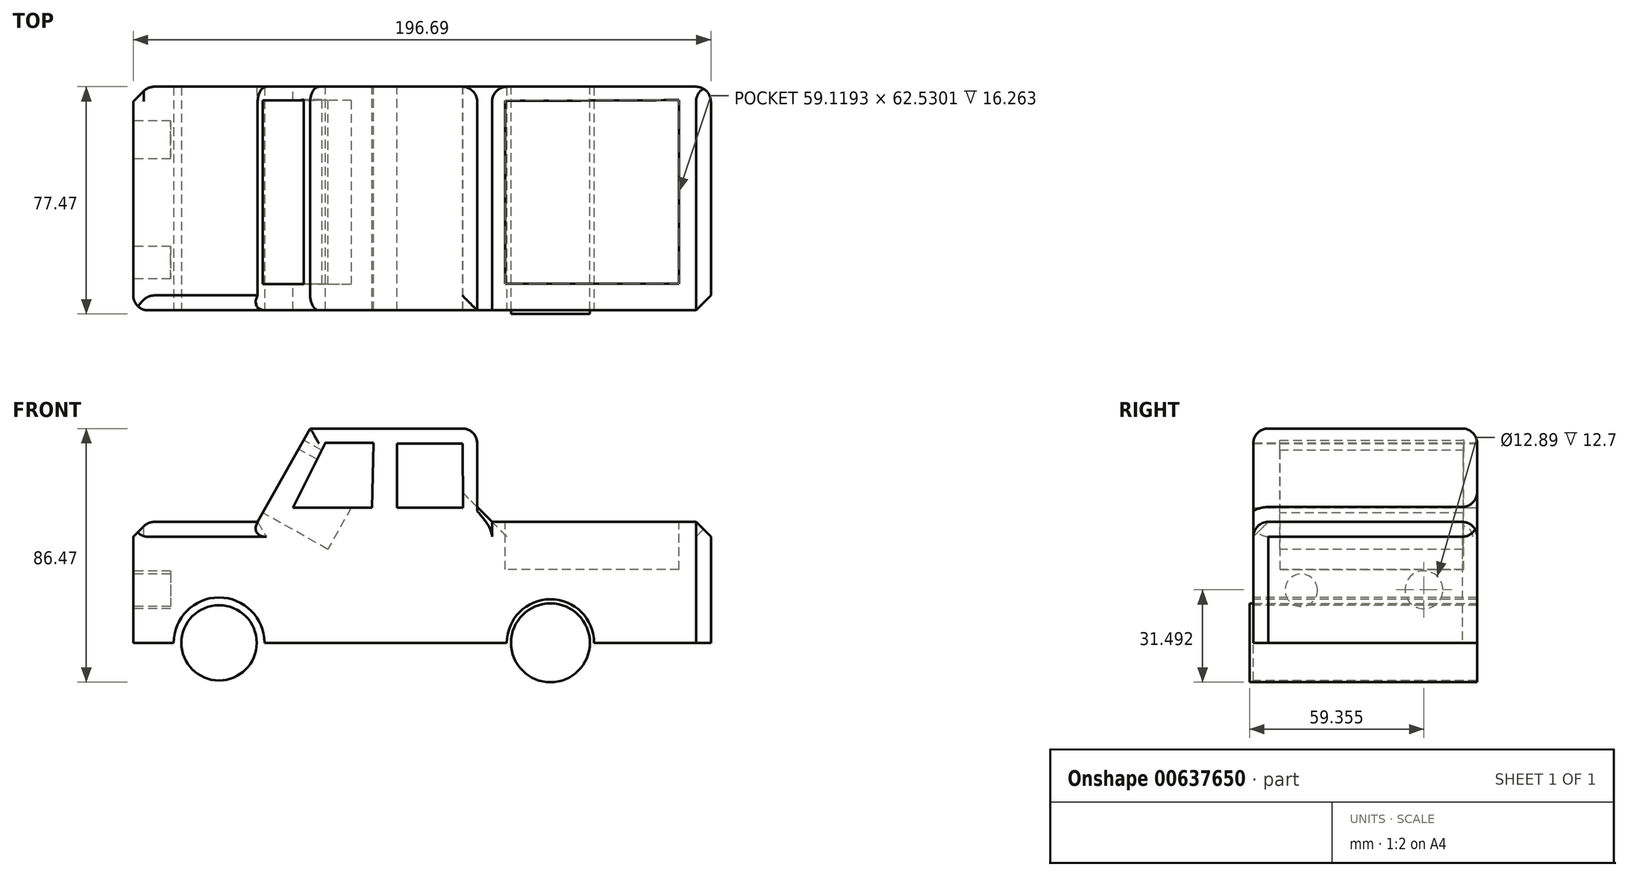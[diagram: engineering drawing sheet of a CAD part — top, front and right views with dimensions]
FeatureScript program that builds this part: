
annotation { "Feature Type Name" : "Feature", "Feature Type Description" : "" }
export const myFeature = defineFeature(function(context is Context, id is Id, definition is map)
    precondition{}
    {
        {
            var Q0;
            Q0=qCreatedBy(makeId("Front.planeOp"),FACE);
            var sketch = newSketch(context, id + "F0", { "sketchPlane" : qUnion([Q0])});
            skLineSegment(sketch, "E0", {"start": v(-75.18, -14.21) * mm, "end": v(-32.83, -14.21) * mm});
            skLineSegment(sketch, "E1", {"start": v(-32.83, -14.21) * mm, "end": v(-14.92, 17.62) * mm});
            skLineSegment(sketch, "E2", {"start": v(-75.18, -14.21) * mm, "end": v(-66.65, -14.21) * mm});
            skLineSegment(sketch, "E3", {"start": v(-14.92, 17.62) * mm, "end": v(41.92, 17.62) * mm});
            skLineSegment(sketch, "E4", {"start": v(41.92, 17.62) * mm, "end": v(41.92, -14.21) * mm});
            skLineSegment(sketch, "E5", {"start": v(41.92, -14.21) * mm, "end": v(-32.83, -14.21) * mm});
            skLineSegment(sketch, "E6", {"start": v(41.92, -14.21) * mm, "end": v(121.5, -14.21) * mm});
            skLineSegment(sketch, "E7", {"start": v(121.5, -14.21) * mm, "end": v(121.5, -37.52) * mm});
            skLineSegment(sketch, "E8", {"start": v(-75.18, -14.21) * mm, "end": v(-75.18, -55.42) * mm});
            skLineSegment(sketch, "E9", {"start": v(-75.18, -55.42) * mm, "end": v(121.5, -55.42) * mm});
            skLineSegment(sketch, "E10", {"start": v(121.5, -55.42) * mm, "end": v(121.5, -37.52) * mm});
            skCircle(sketch, "E11", {"center": v(-45.96, -55.42) * mm, "radius": 13.02 * mm});
            skCircle(sketch, "E12", {"center": v(66.89, -55.42) * mm, "radius": 13.43 * mm});
            skLineSegment(sketch, "E13", {"start": v(-9.74, 12.79) * mm, "end": v(-20.85, -9.38) * mm});
            skLineSegment(sketch, "E14", {"start": v(-9.74, 12.79) * mm, "end": v(6.58, 12.79) * mm});
            skLineSegment(sketch, "E15", {"start": v(-20.85, -9.38) * mm, "end": v(6.1, -9.38) * mm});
            skLineSegment(sketch, "E16", {"start": v(6.1, -9.38) * mm, "end": v(6.58, 12.79) * mm});
            skLineSegment(sketch, "E17", {"start": v(14.61, 12.44) * mm, "end": v(14.61, -9.35) * mm});
            skLineSegment(sketch, "E18", {"start": v(14.61, 12.44) * mm, "end": v(37, 12.44) * mm});
            skLineSegment(sketch, "E19", {"start": v(14.61, -9.35) * mm, "end": v(37.12, -9.35) * mm});
            skLineSegment(sketch, "E20", {"start": v(37, 12.44) * mm, "end": v(37.12, -9.35) * mm});
            skSolve(sketch);
        }
        {
            var Q0;
            Q0 = qSketchRegion(id + "F0", true);
            extrude(context, id + "F1", {"entities" : qUnion([Q0]), "depth" : 76.2 * mm, "offsetDistance" : 25.4 * mm});
        }
        {
            var Q0;
            Q0=makeQuery(id+"F1.opExtrude","CAP_EDGE",EDGE,{"disambiguationData":[OSD([sQuery(id+"F0.wireOp",EDGE,"E3")])],"isStart":false});
            var Q1;
            Q1=makeQuery(id+"F1.opExtrude","SWEPT_EDGE",EDGE,{"disambiguationData":[OSD([sQuery(id+"F0.wireOp",EDGE,"E3"),sQuery(id+"F0.wireOp",EDGE,"E4")])]});
            var Q2;
            Q2=makeQuery(id+"F1.opExtrude","CAP_EDGE",EDGE,{"disambiguationData":[OSD([sQuery(id+"F0.wireOp",EDGE,"E1")])],"isStart":false});
            fillet(context, id + "F2", {"entities" : qUnion([Q0, Q1, Q2]), "radius" : 5.08 * mm, "tangentPropagation" : true, "allowEdgeOverflow" : false});
        }
        {
            var Q0;
            Q0=makeQuery(id+"F1.opExtrude","CAP_EDGE",EDGE,{"disambiguationData":[OSD([sQuery(id+"F0.wireOp",EDGE,"E0"),sQuery(id+"F0.wireOp",EDGE,"E2")])],"isStart":false});
            chamfer(context, id + "F3", {"entities" : qUnion([Q0]), "width" : 5.08 * mm, "tangentPropagation" : true});
        }
        {
            var Q0;
            Q0=makeQuery(id+"F1.opExtrude","CAP_EDGE",EDGE,{"disambiguationData":[OSD([sQuery(id+"F0.wireOp",EDGE,"E8")])],"isStart":false});
            fillet(context, id + "F4", {"entities" : qUnion([Q0]), "radius" : 5.08 * mm, "tangentPropagation" : true, "allowEdgeOverflow" : false});
        }
        {
            var Q0;
            Q0=makeQuery(id+"F1.opExtrude","CAP_EDGE",EDGE,{"disambiguationData":[OSD([sQuery(id+"F0.wireOp",EDGE,"E6")])],"isStart":false});
            fillet(context, id + "F5", {"entities" : qUnion([Q0]), "radius" : 5.08 * mm, "tangentPropagation" : true, "allowEdgeOverflow" : false});
        }
        {
            var Q0;
            {var subQ0=sQuery(id+"F0.wireOp",EDGE,"E6");Q0=makeQuery(id+"F5.opFillet","BLEND_EDGE",EDGE,{"blendedFrom":[makeQuery(id+"F1.opExtrude","CAP_EDGE",EDGE,{"disambiguationData":[OSD([subQ0])],"isStart":false}),makeQuery(id+"F1.opExtrude","SWEPT_FACE",FACE,{"disambiguationData":[OSD([subQ0])]})],"blendedInto":[makeQuery(id+"F1.opExtrude","SWEPT_FACE",FACE,{"disambiguationData":[OSD([subQ0])]})]});}
            var Q1;
            Q1=makeQuery(id+"F5.opFillet","BLEND_FACE",FACE,{"disambiguationData":[OSD([sQuery(id+"F0.wireOp",EDGE,"E6")])]});
            chamfer(context, id + "F6", {"entities" : qUnion([Q0, Q1]), "width" : 5.08 * mm, "tangentPropagation" : true});
        }
        {
            var Q0;
            Q0=qCreatedBy(makeId("Top.planeOp"),FACE);
            var sketch = newSketch(context, id + "F7", { "sketchPlane" : qUnion([Q0])});
            skLineSegment(sketch, "E21", {"start": v(51.5, -4.83) * mm, "end": v(51.5, -67.08) * mm});
            skLineSegment(sketch, "E22", {"start": v(51.5, -67.08) * mm, "end": v(110.62, -67.08) * mm});
            skLineSegment(sketch, "E23", {"start": v(110.62, -67.08) * mm, "end": v(110.62, -4.55) * mm});
            skLineSegment(sketch, "E24", {"start": v(110.62, -4.55) * mm, "end": v(51.5, -4.83) * mm});
            skSolve(sketch);
        }
        {
            var Q0;
            Q0 = qSketchRegion(id + "F7", true);
            extrude(context, id + "F8", {"entities" : qUnion([Q0]), "operationType" : NewBodyOperationType.REMOVE, "oppositeDirection" : true, "depth" : 30.48 * mm, "offsetDistance" : 25.4 * mm});
        }
        {
            var Q0;
            Q0=makeQuery(id+"F1.opExtrude","SWEPT_FACE",FACE,{"disambiguationData":[OSD([sQuery(id+"F0.wireOp",EDGE,"E1")])]});
            var sketch = newSketch(context, id + "F9", { "sketchPlane" : qUnion([Q0])});
            skLineSegment(sketch, "E25", {"start": v(4.69, 0) * mm, "end": v(4.69, -24.9) * mm});
            skLineSegment(sketch, "E26", {"start": v(4.69, -24.9) * mm, "end": v(67.22, -24.9) * mm});
            skLineSegment(sketch, "E27", {"start": v(67.22, -24.9) * mm, "end": v(67.22, 3.48) * mm});
            skLineSegment(sketch, "E28", {"start": v(67.22, 3.48) * mm, "end": v(4.4, 3.48) * mm});
            skLineSegment(sketch, "E29", {"start": v(4.4, 3.48) * mm, "end": v(4.69, 0) * mm});
            skSolve(sketch);
        }
        {
            var Q0;
            Q0=makeQuery(id+"F9.imprint","IMPRINT",FACE,{"disambiguationData":[TD([[makeQuery(id+"F9.imprint","IMPRINT",EDGE,{"derivedFrom":sQuery(id+"F9.wireOp",EDGE,"E25")}),1.0]])]});
            extrude(context, id + "F10", {"entities" : qUnion([Q0]), "operationType" : NewBodyOperationType.REMOVE, "oppositeDirection" : true, "depth" : 25.4 * mm, "offsetDistance" : 25.4 * mm});
        }
        {
            var Q0;
            Q0=sQuery(id+"F0.wireOp",EDGE,"E11");
            extrude(context, id + "F11", {"bodyType" : ToolBodyType.SURFACE, "surfaceEntities" : qUnion([Q0]), "depth" : 76.2 * mm, "offsetDistance" : 25.4 * mm});
        }
        {
            var Q0;
            Q0=makeQuery(id+"F1.opExtrude","CAP_FACE",FACE,{"disambiguationData":[OSD([sQuery(id+"F0.wireOp",EDGE,"E0"),sQuery(id+"F0.wireOp",EDGE,"E1"),sQuery(id+"F0.wireOp",EDGE,"E2"),sQuery(id+"F0.wireOp",EDGE,"E3"),sQuery(id+"F0.wireOp",EDGE,"E4"),sQuery(id+"F0.wireOp",EDGE,"E6"),sQuery(id+"F0.wireOp",EDGE,"E7"),sQuery(id+"F0.wireOp",EDGE,"E8"),sQuery(id+"F0.wireOp",EDGE,"E9"),sQuery(id+"F0.wireOp",EDGE,"E10"),sQuery(id+"F0.wireOp",EDGE,"E11"),sQuery(id+"F0.wireOp",EDGE,"E12"),sQuery(id+"F0.wireOp",EDGE,"E13"),sQuery(id+"F0.wireOp",EDGE,"E14"),sQuery(id+"F0.wireOp",EDGE,"E15"),sQuery(id+"F0.wireOp",EDGE,"E16"),sQuery(id+"F0.wireOp",EDGE,"E17"),sQuery(id+"F0.wireOp",EDGE,"E18"),sQuery(id+"F0.wireOp",EDGE,"E19"),sQuery(id+"F0.wireOp",EDGE,"E20")])],"isStart":false});
            var sketch = newSketch(context, id + "F12", { "sketchPlane" : qUnion([Q0])});
            skCircle(sketch, "E30", {"center": v(-45.96, -55.42) * mm, "radius": 12.82 * mm});
            skCircle(sketch, "E31", {"center": v(-45.96, -55.42) * mm, "radius": 15.45 * mm});
            skSolve(sketch);
        }
        {
            var Q0;
            Q0 = qSketchRegion(id + "F12", true);
            var Q1;
            Q1 = qSketchRegion(id + "F14", true);
            extrude(context, id + "F13", {"entities" : qUnion([Q0, Q1]), "operationType" : NewBodyOperationType.REMOVE, "oppositeDirection" : true, "depth" : 76.2 * mm, "offsetDistance" : 25.4 * mm});
        }
        {
            var Q0;
            {var subQ0=sQuery(id+"F0.wireOp",EDGE,"E18");var subQ1=sQuery(id+"F0.wireOp",EDGE,"E17");var subQ2=sQuery(id+"F0.wireOp",EDGE,"E2");var subQ3=sQuery(id+"F0.wireOp",EDGE,"E0");var subQ4=sQuery(id+"F0.wireOp",EDGE,"E16");var subQ5=sQuery(id+"F0.wireOp",EDGE,"E13");var subQ6=sQuery(id+"F0.wireOp",EDGE,"E12");var subQ7=sQuery(id+"F0.wireOp",EDGE,"E6");var subQ8=sQuery(id+"F0.wireOp",EDGE,"E15");var subQ9=sQuery(id+"F0.wireOp",EDGE,"E4");var subQ10=sQuery(id+"F0.wireOp",EDGE,"E11");var subQ11=sQuery(id+"F0.wireOp",EDGE,"E9");var subQ12=sQuery(id+"F0.wireOp",EDGE,"E1");var subQ13=sQuery(id+"F0.wireOp",EDGE,"E8");var subQ14=sQuery(id+"F0.wireOp",EDGE,"E3");var subQ15=sQuery(id+"F0.wireOp",EDGE,"E10");var subQ16=sQuery(id+"F0.wireOp",EDGE,"E19");var subQ17=sQuery(id+"F0.wireOp",EDGE,"E20");var subQ18=sQuery(id+"F0.wireOp",EDGE,"E7");Q0=makeQuery(id+"F13.boolean.opBoolean","SPLIT",FACE,{"disambiguationData":[TD([makeQuery(id+"F1.opExtrude","SWEPT_FACE",FACE,{"disambiguationData":[OSD([subQ9])]})])],"derivedFrom":makeQuery(id+"F1.opExtrude","CAP_FACE",FACE,{"disambiguationData":[OSD([subQ3,subQ12,subQ2,subQ14,subQ9,subQ7,subQ18,subQ13,subQ11,subQ15,subQ10,subQ6,subQ5,sQuery(id+"F0.wireOp",EDGE,"E14"),subQ8,subQ4,subQ1,subQ0,subQ16,subQ17])],"isStart":false})});}
            var sketch = newSketch(context, id + "F14", { "sketchPlane" : qUnion([Q0])});
            skCircle(sketch, "E32", {"center": v(66.89, -55.42) * mm, "radius": 14.85 * mm});
            skSolve(sketch);
        }
        {
            var Q0;
            Q0 = qSketchRegion(id + "F14", true);
            extrude(context, id + "F15", {"entities" : qUnion([Q0]), "operationType" : NewBodyOperationType.REMOVE, "oppositeDirection" : true, "depth" : 76.2 * mm, "offsetDistance" : 25.4 * mm});
        }
        {
            var Q0;
            Q0 = qSketchRegion(id + "F14", true);
            extrude(context, id + "F16", {"entities" : qUnion([Q0]), "operationType" : NewBodyOperationType.REMOVE, "oppositeDirection" : true, "depth" : 76.2 * mm, "offsetDistance" : 25.4 * mm});
        }
        {
            var Q0;
            {var subQ0=sQuery(id+"F0.wireOp",EDGE,"E12");var subQ1=sQuery(id+"F0.wireOp",EDGE,"E9");var subQ2=makeQuery(id+"F0.imprint","INTERSECT",VERTEX,{"disambiguationData":[OD(0.0)],"derivedFrom":[subQ1,subQ0]});Q0=makeQuery(id+"F0.imprint","IMPRINT",FACE,{"disambiguationData":[TD([[makeQuery(id+"F0.imprint","IMPRINT",EDGE,{"disambiguationData":[TD([[subQ2,-1.0]])],"derivedFrom":subQ1}),-1.0]])]});}
            var Q1;
            {var subQ0=sQuery(id+"F0.wireOp",EDGE,"E12");var subQ1=sQuery(id+"F0.wireOp",EDGE,"E9");var subQ2=makeQuery(id+"F0.imprint","INTERSECT",VERTEX,{"disambiguationData":[OD(0.0)],"derivedFrom":[subQ1,subQ0]});Q1=makeQuery(id+"F0.imprint","IMPRINT",FACE,{"disambiguationData":[TD([[makeQuery(id+"F0.imprint","IMPRINT",EDGE,{"disambiguationData":[TD([[subQ2,-1.0]])],"derivedFrom":subQ1}),1.0]])]});}
            extrude(context, id + "F17", {"entities" : qUnion([Q0, Q1]), "depth" : 77.47 * mm, "offsetDistance" : 25.4 * mm});
        }
        {
            var Q0;
            Q0=makeQuery(id+"F1.opExtrude","CAP_EDGE",EDGE,{"disambiguationData":[OSD([sQuery(id+"F0.wireOp",EDGE,"E1")])],"isStart":true});
            var Q1;
            Q1=makeQuery(id+"F1.opExtrude","CAP_EDGE",EDGE,{"disambiguationData":[OSD([sQuery(id+"F0.wireOp",EDGE,"E3")])],"isStart":true});
            var Q2;
            Q2=makeQuery(id+"F1.opExtrude","CAP_EDGE",EDGE,{"disambiguationData":[OSD([sQuery(id+"F0.wireOp",EDGE,"E0"),sQuery(id+"F0.wireOp",EDGE,"E2")])],"isStart":true});
            fillet(context, id + "F18", {"entities" : qUnion([Q0, Q1, Q2]), "radius" : 5.08 * mm, "tangentPropagation" : true, "allowEdgeOverflow" : false});
        }
        {
            var Q0;
            Q0=makeQuery(id+"F1.opExtrude","CAP_EDGE",EDGE,{"disambiguationData":[OSD([sQuery(id+"F0.wireOp",EDGE,"E8")])],"isStart":true});
            chamfer(context, id + "F19", {"entities" : qUnion([Q0]), "width" : 5.08 * mm, "tangentPropagation" : true});
        }
        {
            var Q0;
            Q0=makeQuery(id+"F1.opExtrude","CAP_EDGE",EDGE,{"disambiguationData":[OSD([sQuery(id+"F0.wireOp",EDGE,"E6")])],"isStart":true});
            var Q1;
            {var subQ0=sQuery(id+"F0.wireOp",EDGE,"E7");var subQ1=sQuery(id+"F0.wireOp",EDGE,"E6");var subQ2=sQuery(id+"F0.wireOp",EDGE,"E4");var subQ3=sQuery(id+"F0.wireOp",EDGE,"E20");var subQ4=sQuery(id+"F0.wireOp",EDGE,"E19");var subQ5=sQuery(id+"F0.wireOp",EDGE,"E18");var subQ6=sQuery(id+"F0.wireOp",EDGE,"E17");var subQ7=sQuery(id+"F0.wireOp",EDGE,"E16");var subQ8=sQuery(id+"F0.wireOp",EDGE,"E15");var subQ9=sQuery(id+"F0.wireOp",EDGE,"E14");var subQ10=sQuery(id+"F0.wireOp",EDGE,"E13");var subQ11=sQuery(id+"F0.wireOp",EDGE,"E12");var subQ12=sQuery(id+"F0.wireOp",EDGE,"E3");var subQ13=sQuery(id+"F0.wireOp",EDGE,"E1");var subQ14=sQuery(id+"F0.wireOp",EDGE,"E2");var subQ15=sQuery(id+"F0.wireOp",EDGE,"E0");var subQ16=sQuery(id+"F0.wireOp",EDGE,"E10");var subQ17=sQuery(id+"F0.wireOp",EDGE,"E8");var subQ18=sQuery(id+"F0.wireOp",EDGE,"E9");var subQ19=sQuery(id+"F0.wireOp",EDGE,"E11");Q1=makeQuery(id+"F18.opFillet","BLEND_EDGE",EDGE,{"blendedFrom":[makeQuery(id+"F1.opExtrude","CAP_EDGE",EDGE,{"disambiguationData":[OSD([subQ13])],"isStart":true}),makeQuery(id+"F13.boolean.opBoolean","SPLIT",FACE,{"disambiguationData":[TD([makeQuery(id+"F1.opExtrude","SWEPT_FACE",FACE,{"disambiguationData":[OSD([subQ13])]})])],"derivedFrom":makeQuery(id+"F1.opExtrude","CAP_FACE",FACE,{"disambiguationData":[OSD([subQ15,subQ13,subQ14,subQ12,subQ2,subQ1,subQ0,subQ17,subQ18,subQ16,subQ19,subQ11,subQ10,subQ9,subQ8,subQ7,subQ6,subQ5,subQ4,subQ3])],"isStart":true})})],"blendedInto":[makeQuery(id+"F13.boolean.opBoolean","SPLIT",FACE,{"disambiguationData":[TD([makeQuery(id+"F1.opExtrude","SWEPT_FACE",FACE,{"disambiguationData":[OSD([subQ13])]})])],"derivedFrom":makeQuery(id+"F1.opExtrude","CAP_FACE",FACE,{"disambiguationData":[OSD([subQ15,subQ13,subQ14,subQ12,subQ2,subQ1,subQ0,subQ17,subQ18,subQ16,subQ19,subQ11,subQ10,subQ9,subQ8,subQ7,subQ6,subQ5,subQ4,subQ3])],"isStart":true})})]});}
            fillet(context, id + "F20", {"entities" : qUnion([Q0, Q1]), "radius" : 5.08 * mm, "tangentPropagation" : true, "allowEdgeOverflow" : false});
        }
        {
            var Q0;
            Q0=makeQuery(id+"F1.opExtrude","CAP_EDGE",EDGE,{"disambiguationData":[OSD([sQuery(id+"F0.wireOp",EDGE,"E7"),sQuery(id+"F0.wireOp",EDGE,"E10")])],"isStart":true});
            fillet(context, id + "F21", {"entities" : qUnion([Q0]), "radius" : 5.08 * mm, "tangentPropagation" : true, "allowEdgeOverflow" : false});
        }
        {
            var Q0;
            {var subQ0=sQuery(id+"F0.wireOp",EDGE,"E7");var subQ1=sQuery(id+"F0.wireOp",EDGE,"E6");var subQ2=sQuery(id+"F0.wireOp",EDGE,"E4");var subQ3=sQuery(id+"F0.wireOp",EDGE,"E20");var subQ4=sQuery(id+"F0.wireOp",EDGE,"E19");var subQ5=sQuery(id+"F0.wireOp",EDGE,"E18");var subQ6=sQuery(id+"F0.wireOp",EDGE,"E17");var subQ7=sQuery(id+"F0.wireOp",EDGE,"E16");var subQ8=sQuery(id+"F0.wireOp",EDGE,"E15");var subQ9=sQuery(id+"F0.wireOp",EDGE,"E14");var subQ10=sQuery(id+"F0.wireOp",EDGE,"E13");var subQ11=sQuery(id+"F0.wireOp",EDGE,"E12");var subQ12=sQuery(id+"F0.wireOp",EDGE,"E3");var subQ13=sQuery(id+"F0.wireOp",EDGE,"E1");var subQ14=sQuery(id+"F0.wireOp",EDGE,"E2");var subQ15=sQuery(id+"F0.wireOp",EDGE,"E0");var subQ16=sQuery(id+"F0.wireOp",EDGE,"E10");var subQ17=sQuery(id+"F0.wireOp",EDGE,"E8");var subQ18=sQuery(id+"F0.wireOp",EDGE,"E9");var subQ19=sQuery(id+"F0.wireOp",EDGE,"E11");Q0=makeQuery(id+"F19.opChamfer","BLEND_EDGE",EDGE,{"blendedFrom":[makeQuery(id+"F1.opExtrude","CAP_EDGE",EDGE,{"disambiguationData":[OSD([subQ17])],"isStart":true}),makeQuery(id+"F13.boolean.opBoolean","SPLIT",FACE,{"disambiguationData":[TD([makeQuery(id+"F1.opExtrude","SWEPT_FACE",FACE,{"disambiguationData":[OSD([subQ13])]})])],"derivedFrom":makeQuery(id+"F1.opExtrude","CAP_FACE",FACE,{"disambiguationData":[OSD([subQ15,subQ13,subQ14,subQ12,subQ2,subQ1,subQ0,subQ17,subQ18,subQ16,subQ19,subQ11,subQ10,subQ9,subQ8,subQ7,subQ6,subQ5,subQ4,subQ3])],"isStart":true})})],"blendedInto":[makeQuery(id+"F13.boolean.opBoolean","SPLIT",FACE,{"disambiguationData":[TD([makeQuery(id+"F1.opExtrude","SWEPT_FACE",FACE,{"disambiguationData":[OSD([subQ13])]})])],"derivedFrom":makeQuery(id+"F1.opExtrude","CAP_FACE",FACE,{"disambiguationData":[OSD([subQ15,subQ13,subQ14,subQ12,subQ2,subQ1,subQ0,subQ17,subQ18,subQ16,subQ19,subQ11,subQ10,subQ9,subQ8,subQ7,subQ6,subQ5,subQ4,subQ3])],"isStart":true})})]});}
            fillet(context, id + "F22", {"entities" : qUnion([Q0]), "radius" : 5.08 * mm, "tangentPropagation" : true, "allowEdgeOverflow" : false});
        }
        {
            var Q0;
            Q0=makeQuery(id+"F1.opExtrude","SWEPT_FACE",FACE,{"disambiguationData":[OSD([sQuery(id+"F0.wireOp",EDGE,"E8")])]});
            var sketch = newSketch(context, id + "F23", { "sketchPlane" : qUnion([Q0])});
            skCircle(sketch, "E33", {"center": v(18.11, -37.36) * mm, "radius": 6.45 * mm});
            skPoint(sketch, "E33.centerSnap0", {"position": v(71.12, -37.36) * mm});
            skSolve(sketch);
        }
        {
            var Q0;
            Q0 = qSketchRegion(id + "F23", true);
            extrude(context, id + "F24", {"entities" : qUnion([Q0]), "operationType" : NewBodyOperationType.REMOVE, "oppositeDirection" : true, "depth" : 12.7 * mm, "offsetDistance" : 25.4 * mm});
        }
        {
            var Q0;
            Q0=makeQuery(id+"F1.opExtrude","SWEPT_FACE",FACE,{"disambiguationData":[OSD([sQuery(id+"F0.wireOp",EDGE,"E8")])]});
            var sketch = newSketch(context, id + "F25", { "sketchPlane" : qUnion([Q0])});
            skCircle(sketch, "E34", {"center": v(59.9, -37.52) * mm, "radius": 5.52 * mm});
            skSolve(sketch);
        }
        {
            var Q0;
            Q0 = qSketchRegion(id + "F25", true);
            extrude(context, id + "F26", {"entities" : qUnion([Q0]), "operationType" : NewBodyOperationType.REMOVE, "oppositeDirection" : true, "depth" : 12.7 * mm, "offsetDistance" : 25.4 * mm});
        }
    });
